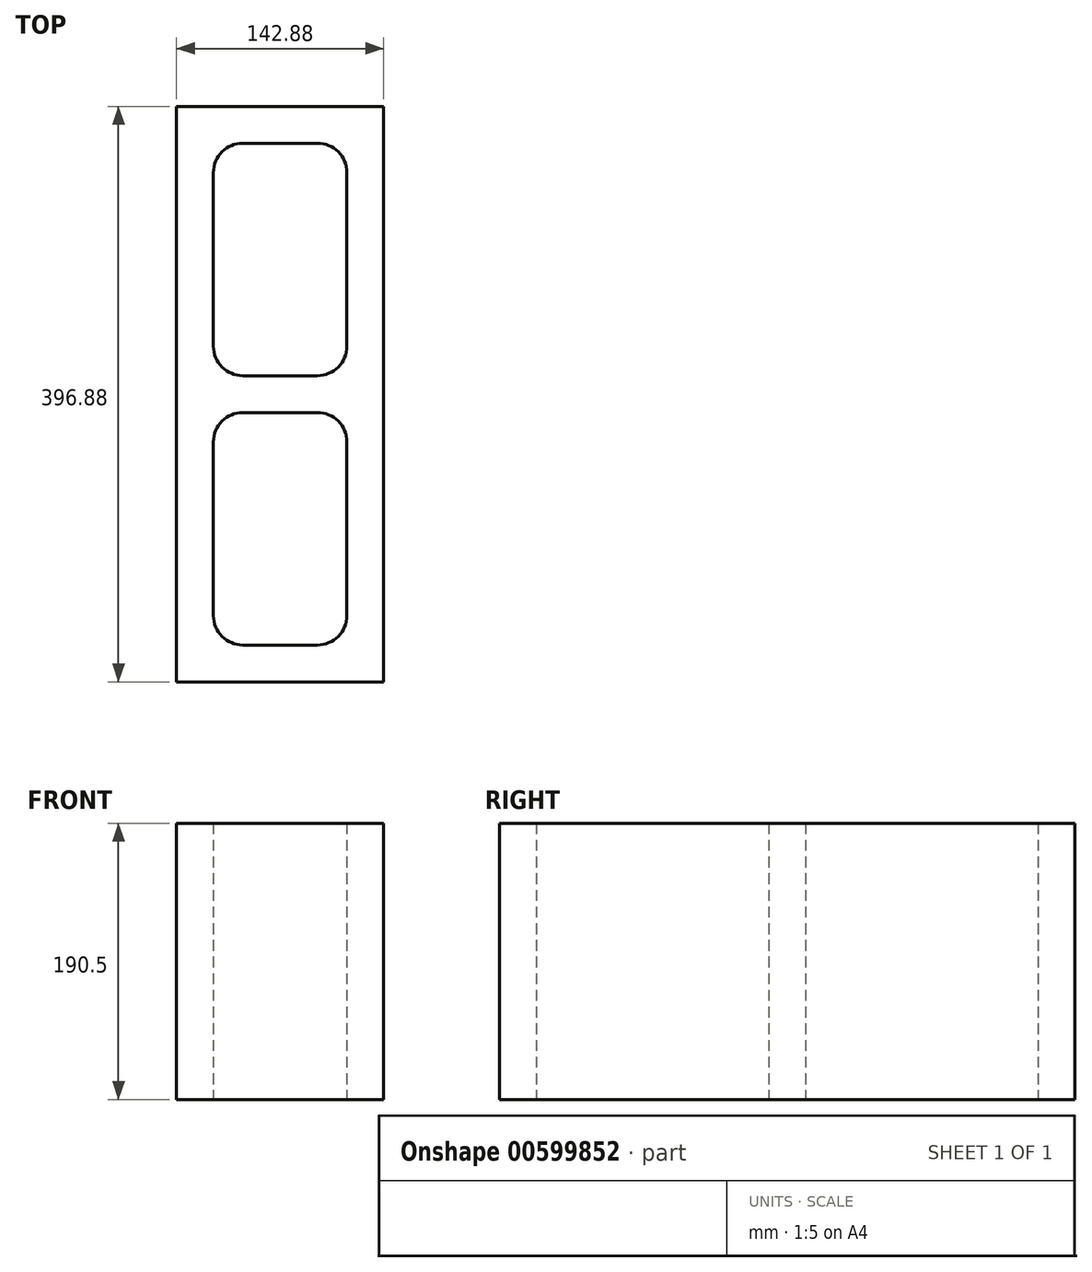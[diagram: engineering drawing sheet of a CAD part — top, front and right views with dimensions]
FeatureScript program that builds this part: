
annotation { "Feature Type Name" : "Feature", "Feature Type Description" : "" }
export const myFeature = defineFeature(function(context is Context, id is Id, definition is map)
    precondition{}
    {
        {
            var Q0;
            Q0=qCreatedBy(makeId("Top.planeOp"),FACE);
            var sketch = newSketch(context, id + "F0", { "sketchPlane" : qUnion([Q0])});
            skLineSegment(sketch, "E0.bottom", {"start": v(71.44, 198.44) * mm, "end": v(-71.44, 198.44) * mm});
            skLineSegment(sketch, "E0.top", {"start": v(71.44, -198.44) * mm, "end": v(-71.44, -198.44) * mm});
            skLineSegment(sketch, "E0.left", {"start": v(71.44, 198.44) * mm, "end": v(71.44, -198.44) * mm});
            skLineSegment(sketch, "E0.right", {"start": v(-71.44, 198.44) * mm, "end": v(-71.44, -198.44) * mm});
            skPoint(sketch, "E0.middle", {"position": v(0, 0) * mm});
            skLineSegment(sketch, "E1.bottom", {"start": v(25.72, 12.7) * mm, "end": v(-25.72, 12.7) * mm});
            skLineSegment(sketch, "E1.top", {"start": v(25.72, 173.04) * mm, "end": v(-25.72, 173.04) * mm});
            skLineSegment(sketch, "E1.left", {"start": v(46.04, 33.02) * mm, "end": v(46.04, 152.72) * mm});
            skLineSegment(sketch, "E1.right", {"start": v(-46.04, 33.02) * mm, "end": v(-46.04, 152.72) * mm});
            skPoint(sketch, "E1.middle", {"position": v(0, 92.87) * mm});
            skLineSegment(sketch, "E2", {"start": v(-132.31, 0) * mm, "end": v(175.7, 0) * mm, "construction": true});
            skPoint(sketch, "E2.endSnap0", {"position": v(71.44, 0) * mm});
            skPoint(sketch, "E3.visualSharp", {"position": v(-46.04, 173.04) * mm});
            skArc(sketch, "E3.filletArc", {"start": v(-25.72, 173.04) * mm, "mid": v(-40.09, 167.09) * mm, "end": v(-46.04, 152.72) * mm});
            skPoint(sketch, "E4.visualSharp", {"position": v(46.04, 173.04) * mm});
            skArc(sketch, "E4.filletArc", {"start": v(46.04, 152.72) * mm, "mid": v(40.09, 167.09) * mm, "end": v(25.72, 173.04) * mm});
            skPoint(sketch, "E5.visualSharp", {"position": v(46.04, 12.7) * mm});
            skArc(sketch, "E5.filletArc", {"start": v(25.72, 12.7) * mm, "mid": v(40.09, 18.65) * mm, "end": v(46.04, 33.02) * mm});
            skPoint(sketch, "E6.visualSharp", {"position": v(-46.04, 12.7) * mm});
            skArc(sketch, "E6.filletArc", {"start": v(-46.04, 33.02) * mm, "mid": v(-40.09, 18.65) * mm, "end": v(-25.72, 12.7) * mm});
            skPoint(sketch, "E7.MirrorP", {"position": v(0, -92.87) * mm});
            skArc(sketch, "E8.MirrorCS", {"start": v(-46.04, -33.02) * mm, "mid": v(-40.09, -18.65) * mm, "end": v(-25.72, -12.7) * mm});
            skPoint(sketch, "E9.MirrorP", {"position": v(46.04, -173.04) * mm});
            skArc(sketch, "E10.MirrorCS", {"start": v(46.04, -152.72) * mm, "mid": v(40.09, -167.09) * mm, "end": v(25.72, -173.04) * mm});
            skLineSegment(sketch, "E11.MirrorCS", {"start": v(25.72, -12.7) * mm, "end": v(-25.72, -12.7) * mm});
            skArc(sketch, "E12.MirrorCS", {"start": v(-25.72, -173.04) * mm, "mid": v(-40.09, -167.09) * mm, "end": v(-46.04, -152.72) * mm});
            skLineSegment(sketch, "E13.MirrorCS", {"start": v(25.72, -173.04) * mm, "end": v(-25.72, -173.04) * mm});
            skPoint(sketch, "E14.MirrorP", {"position": v(-46.04, -12.7) * mm});
            skPoint(sketch, "E15.MirrorP", {"position": v(46.04, -12.7) * mm});
            skArc(sketch, "E16.MirrorCS", {"start": v(25.72, -12.7) * mm, "mid": v(40.09, -18.65) * mm, "end": v(46.04, -33.02) * mm});
            skLineSegment(sketch, "E17.MirrorCS", {"start": v(46.04, -33.02) * mm, "end": v(46.04, -152.72) * mm});
            skLineSegment(sketch, "E18.MirrorCS", {"start": v(-46.04, -33.02) * mm, "end": v(-46.04, -152.72) * mm});
            skPoint(sketch, "E19.MirrorP", {"position": v(-46.04, -173.04) * mm});
            skSolve(sketch);
        }
        {
            var Q0;
            Q0=makeQuery(id+"F0.imprint","IMPRINT",FACE,{"disambiguationData":[TD([[makeQuery(id+"F0.imprint","IMPRINT",EDGE,{"derivedFrom":sQuery(id+"F0.wireOp",EDGE,"E0.bottom")}),1.0]])]});
            extrude(context, id + "F1", {"entities" : qUnion([Q0]), "endBound" : BoundingType.SYMMETRIC, "depth" : 190.5 * mm, "offsetDistance" : 25.4 * mm});
        }
    });
